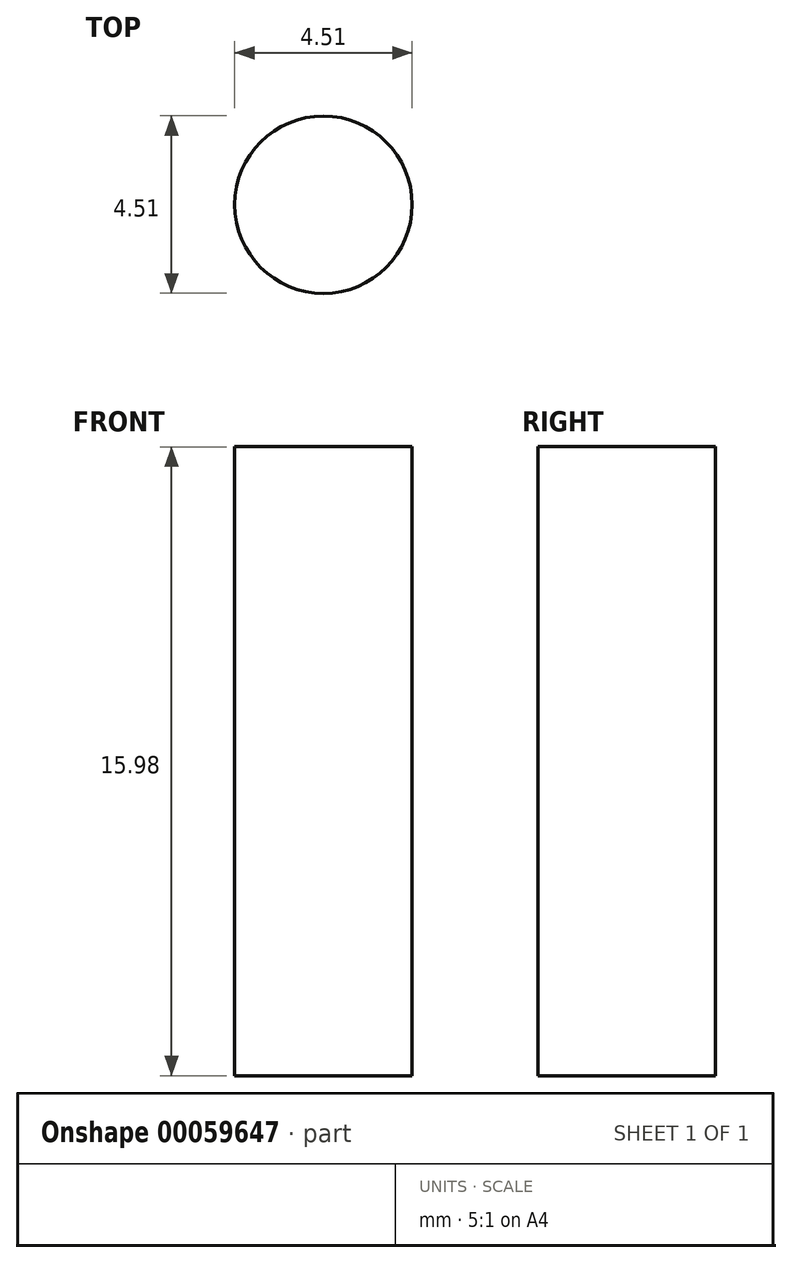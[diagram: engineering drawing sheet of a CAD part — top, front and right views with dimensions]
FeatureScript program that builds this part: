
annotation { "Feature Type Name" : "Feature", "Feature Type Description" : "" }
export const myFeature = defineFeature(function(context is Context, id is Id, definition is map)
    precondition{}
    {
        {
            var Q0;
            Q0=qCreatedBy(makeId("Top.planeOp"),FACE);
            var sketch = newSketch(context, id + "F0", { "sketchPlane" : qUnion([Q0])});
            skCircle(sketch, "E0", {"center": v(-51.53, 31.08) * mm, "radius": 2.25 * mm});
            skSolve(sketch);
        }
        {
            var Q0;
            Q0 = qSketchRegion(id + "F0", true);
            extrude(context, id + "F1", {"entities" : qUnion([Q0]), "depth" : 15.98 * mm});
        }
    });
